# Revit family: FU_Sandler_Dixie_2-1
name_source: partatom
category: Furniture
units: mm (PartAtom-declared; Revit-internal decimal feet)

## family parameters
Always vertical = Yes
Cut with Voids When Loaded = No
OmniClass Number = 23.40.20.00
OmniClass Title = General Furniture and Specialties
Room Calculation Point = No
Shared = No
Work Plane-Based = No

## types (1)
- FU_Sandler_Dixie_2-1
    Back Fabric = Fabric White
    Default Elevation = 0 mm  [stored 0 ft]
    Depth = 510 mm  [stored 1.67323 ft]
    Description = Armchair with upholstered seat and back and wooden frame in natural beech.
    Height = 795 mm  [stored 2.60827 ft]
    Manufacturer = Sandler
    Model = Dixie 2.1
    Seat Fabric = Leather, Dark Brown
    Seat Height = 480 mm  [stored 1.5748 ft]
    URL = https://www.sandlerseating.com
    Width = 560 mm  [stored 1.83727 ft]
    Wood Frame = Natural Beech

note: [stored X ft] marks values corroborated as IEEE doubles in the binary element streams (Revit-internal decimal feet)

## geometry (parser evidence)
native form markers: Sweep x6
no freeform markers — native parametric forms only
